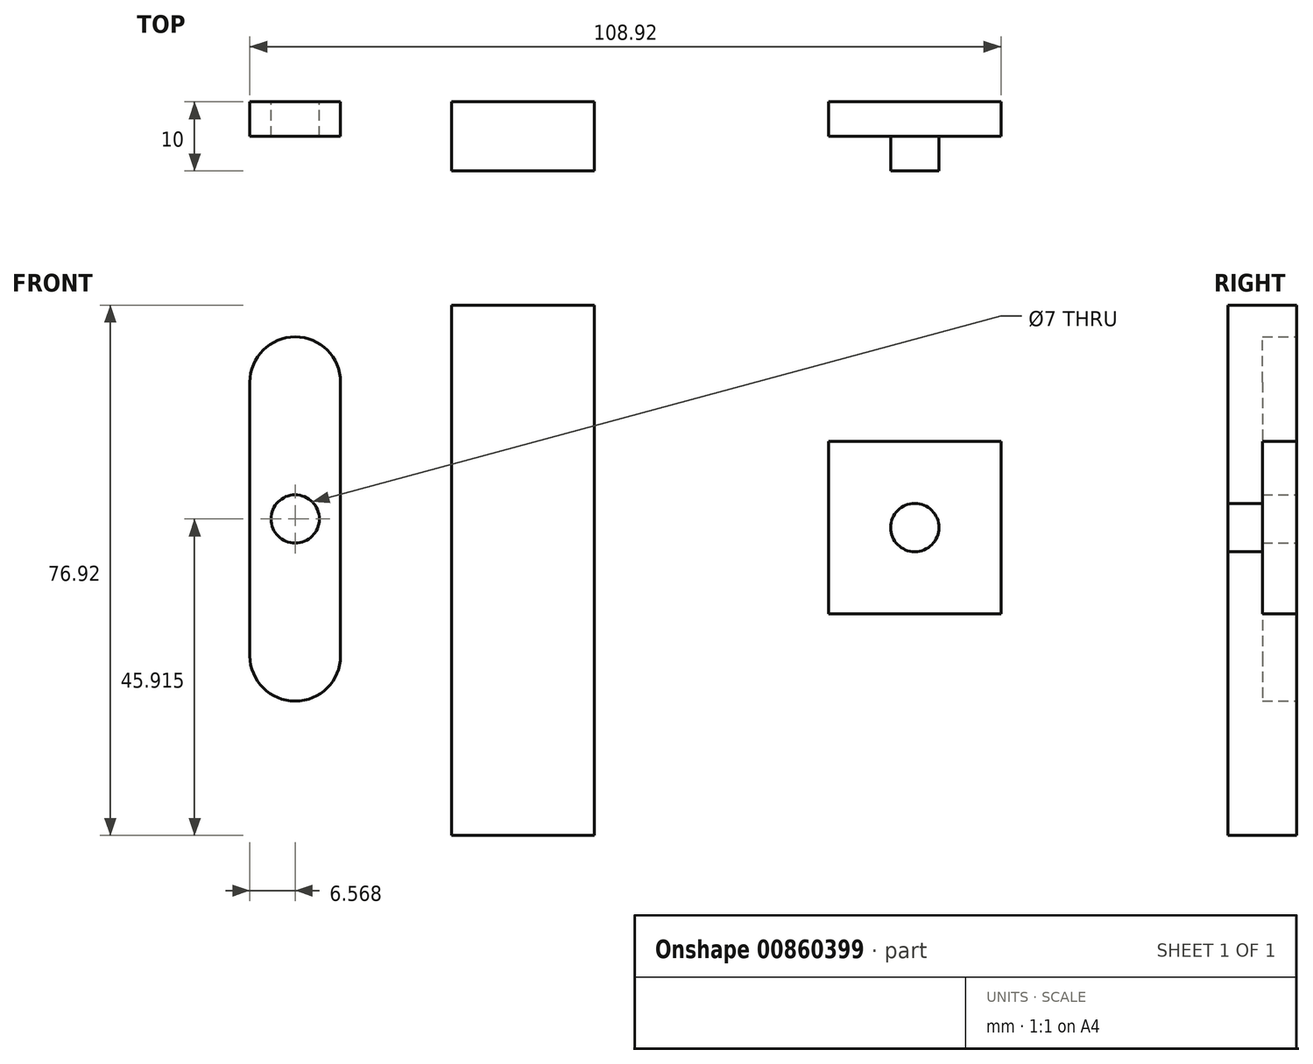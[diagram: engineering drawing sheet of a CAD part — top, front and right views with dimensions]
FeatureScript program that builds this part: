
annotation { "Feature Type Name" : "Feature", "Feature Type Description" : "" }
export const myFeature = defineFeature(function(context is Context, id is Id, definition is map)
    precondition{}
    {
        {
            var Q0;
            Q0=qCreatedBy(makeId("Front.planeOp"),FACE);
            var sketch = newSketch(context, id + "F0", { "sketchPlane" : qUnion([Q0])});
            skLineSegment(sketch, "E0", {"start": v(-60.7, 49.25) * mm, "end": v(-60.7, 9.54) * mm});
            skLineSegment(sketch, "E1", {"start": v(-60.7, 9.54) * mm, "end": v(-47.56, 9.54) * mm, "construction": true});
            skLineSegment(sketch, "E2", {"start": v(-47.56, 9.54) * mm, "end": v(-47.56, 49.25) * mm});
            skLineSegment(sketch, "E3", {"start": v(-47.56, 49.25) * mm, "end": v(-60.7, 49.25) * mm, "construction": true});
            skArc(sketch, "E4", {"start": v(-47.56, 49.25) * mm, "mid": v(-54.13, 55.82) * mm, "end": v(-60.7, 49.25) * mm});
            skArc(sketch, "E5", {"start": v(-60.7, 9.54) * mm, "mid": v(-54.13, 2.97) * mm, "end": v(-47.56, 9.54) * mm});
            skLineSegment(sketch, "E6", {"start": v(-60.7, 49.25) * mm, "end": v(-60.7, 29.4) * mm});
            skLineSegment(sketch, "E7", {"start": v(-60.7, 29.4) * mm, "end": v(-47.56, 29.4) * mm, "construction": true});
            skCircle(sketch, "E8", {"center": v(-54.13, 29.4) * mm, "radius": 3.5 * mm});
            skSolve(sketch);
        }
        {
            var Q0;
            Q0=makeQuery(id+"F0.imprint","IMPRINT",FACE,{"disambiguationData":[TD([[makeQuery(id+"F0.imprint","IMPRINT",EDGE,{"derivedFrom":sQuery(id+"F0.wireOp",EDGE,"E0")}),1.0]])]});
            extrude(context, id + "F1", {"entities" : qUnion([Q0]), "depth" : 5 * mm, "offsetDistance" : 25 * mm});
        }
        {
            var Q0;
            Q0=qCreatedBy(makeId("Front.planeOp"),FACE);
            var sketch = newSketch(context, id + "F2", { "sketchPlane" : qUnion([Q0])});
            skLineSegment(sketch, "E9.bottom", {"start": v(-31.43, 60.4) * mm, "end": v(-10.76, 60.4) * mm});
            skLineSegment(sketch, "E9.top", {"start": v(-31.43, -16.52) * mm, "end": v(-10.76, -16.52) * mm});
            skLineSegment(sketch, "E9.left", {"start": v(-31.43, 60.4) * mm, "end": v(-31.43, -16.52) * mm});
            skLineSegment(sketch, "E9.right", {"start": v(-10.76, 60.4) * mm, "end": v(-10.76, -16.52) * mm});
            skSolve(sketch);
        }
        {
            var Q0;
            Q0 = qSketchRegion(id + "F2", true);
            extrude(context, id + "F3", {"entities" : qUnion([Q0]), "depth" : 10 * mm, "offsetDistance" : 25 * mm});
        }
        {
            var Q0;
            Q0=qCreatedBy(makeId("Front.planeOp"),FACE);
            var sketch = newSketch(context, id + "F4", { "sketchPlane" : qUnion([Q0])});
            skLineSegment(sketch, "E10.bottom", {"start": v(23.22, 40.65) * mm, "end": v(48.22, 40.65) * mm});
            skLineSegment(sketch, "E10.top", {"start": v(23.22, 15.65) * mm, "end": v(48.22, 15.65) * mm});
            skLineSegment(sketch, "E10.left", {"start": v(23.22, 40.65) * mm, "end": v(23.22, 15.65) * mm});
            skLineSegment(sketch, "E10.right", {"start": v(48.22, 40.65) * mm, "end": v(48.22, 15.65) * mm});
            skLineSegment(sketch, "E11", {"start": v(23.22, 40.65) * mm, "end": v(48.22, 15.65) * mm});
            skLineSegment(sketch, "E12", {"start": v(23.22, 15.65) * mm, "end": v(48.22, 40.65) * mm});
            skCircle(sketch, "E13", {"center": v(35.72, 28.15) * mm, "radius": 3.5 * mm});
            skSolve(sketch);
        }
        {
            var Q0;
            {var subQ0=sQuery(id+"F4.wireOp",EDGE,"E10.bottom");Q0=makeQuery(id+"F4.imprint","IMPRINT",FACE,{"disambiguationData":[TD([[makeQuery(id+"F4.imprint","IMPRINT",EDGE,{"derivedFrom":subQ0}),-1.0]])]});}
            var Q1;
            {var subQ0=sQuery(id+"F4.wireOp",EDGE,"E10.left");Q1=makeQuery(id+"F4.imprint","IMPRINT",FACE,{"disambiguationData":[TD([[makeQuery(id+"F4.imprint","IMPRINT",EDGE,{"derivedFrom":subQ0}),1.0]])]});}
            var Q2;
            {var subQ0=sQuery(id+"F4.wireOp",EDGE,"E10.top");Q2=makeQuery(id+"F4.imprint","IMPRINT",FACE,{"disambiguationData":[TD([[makeQuery(id+"F4.imprint","IMPRINT",EDGE,{"derivedFrom":subQ0}),1.0]])]});}
            var Q3;
            {var subQ0=sQuery(id+"F4.wireOp",EDGE,"E10.right");Q3=makeQuery(id+"F4.imprint","IMPRINT",FACE,{"disambiguationData":[TD([[makeQuery(id+"F4.imprint","IMPRINT",EDGE,{"derivedFrom":subQ0}),-1.0]])]});}
            var Q4;
            {var subQ0=sQuery(id+"F4.wireOp",EDGE,"E13");var subQ1=sQuery(id+"F4.wireOp",EDGE,"E11");var subQ2=makeQuery(id+"F4.imprint","INTERSECT",VERTEX,{"disambiguationData":[OD(0.0)],"derivedFrom":[subQ1,subQ0]});Q4=makeQuery(id+"F4.imprint","IMPRINT",FACE,{"disambiguationData":[TD([[makeQuery(id+"F4.imprint","IMPRINT",EDGE,{"disambiguationData":[TD([[subQ2,-1.0]])],"derivedFrom":subQ1}),-1.0]])]});}
            var Q5;
            {var subQ0=sQuery(id+"F4.wireOp",EDGE,"E13");var subQ1=sQuery(id+"F4.wireOp",EDGE,"E11");var subQ2=makeQuery(id+"F4.imprint","INTERSECT",VERTEX,{"disambiguationData":[OD(0.0)],"derivedFrom":[subQ1,subQ0]});Q5=makeQuery(id+"F4.imprint","IMPRINT",FACE,{"disambiguationData":[TD([[makeQuery(id+"F4.imprint","IMPRINT",EDGE,{"disambiguationData":[TD([[subQ2,-1.0]])],"derivedFrom":subQ1}),1.0]])]});}
            var Q6;
            {var subQ0=sQuery(id+"F4.wireOp",EDGE,"E12");var subQ1=sQuery(id+"F4.wireOp",EDGE,"E11");var subQ2=makeQuery(id+"F4.imprint","INTERSECT",VERTEX,{"derivedFrom":[subQ1,subQ0]});Q6=makeQuery(id+"F4.imprint","IMPRINT",FACE,{"disambiguationData":[TD([[makeQuery(id+"F4.imprint","IMPRINT",EDGE,{"disambiguationData":[TD([[subQ2,-1.0]])],"derivedFrom":subQ1}),1.0]])]});}
            var Q7;
            {var subQ0=sQuery(id+"F4.wireOp",EDGE,"E12");var subQ1=sQuery(id+"F4.wireOp",EDGE,"E11");var subQ2=makeQuery(id+"F4.imprint","INTERSECT",VERTEX,{"derivedFrom":[subQ1,subQ0]});Q7=makeQuery(id+"F4.imprint","IMPRINT",FACE,{"disambiguationData":[TD([[makeQuery(id+"F4.imprint","IMPRINT",EDGE,{"disambiguationData":[TD([[subQ2,-1.0]])],"derivedFrom":subQ1}),-1.0]])]});}
            extrude(context, id + "F5", {"entities" : qUnion([Q0, Q1, Q2, Q3, Q4, Q5, Q6, Q7]), "depth" : 5 * mm, "offsetDistance" : 25 * mm});
        }
        {
            var Q0;
            {var subQ0=sQuery(id+"F4.wireOp",EDGE,"E13");var subQ1=sQuery(id+"F4.wireOp",EDGE,"E11");var subQ2=makeQuery(id+"F4.imprint","INTERSECT",VERTEX,{"disambiguationData":[OD(0.0)],"derivedFrom":[subQ1,subQ0]});Q0=makeQuery(id+"F4.imprint","IMPRINT",FACE,{"disambiguationData":[TD([[makeQuery(id+"F4.imprint","IMPRINT",EDGE,{"disambiguationData":[TD([[subQ2,-1.0]])],"derivedFrom":subQ1}),1.0]])]});}
            var Q1;
            {var subQ0=sQuery(id+"F4.wireOp",EDGE,"E12");var subQ1=sQuery(id+"F4.wireOp",EDGE,"E11");var subQ2=makeQuery(id+"F4.imprint","INTERSECT",VERTEX,{"derivedFrom":[subQ1,subQ0]});Q1=makeQuery(id+"F4.imprint","IMPRINT",FACE,{"disambiguationData":[TD([[makeQuery(id+"F4.imprint","IMPRINT",EDGE,{"disambiguationData":[TD([[subQ2,-1.0]])],"derivedFrom":subQ1}),1.0]])]});}
            var Q2;
            {var subQ0=sQuery(id+"F4.wireOp",EDGE,"E12");var subQ1=sQuery(id+"F4.wireOp",EDGE,"E11");var subQ2=makeQuery(id+"F4.imprint","INTERSECT",VERTEX,{"derivedFrom":[subQ1,subQ0]});Q2=makeQuery(id+"F4.imprint","IMPRINT",FACE,{"disambiguationData":[TD([[makeQuery(id+"F4.imprint","IMPRINT",EDGE,{"disambiguationData":[TD([[subQ2,-1.0]])],"derivedFrom":subQ1}),-1.0]])]});}
            var Q3;
            {var subQ0=sQuery(id+"F4.wireOp",EDGE,"E13");var subQ1=sQuery(id+"F4.wireOp",EDGE,"E11");var subQ2=makeQuery(id+"F4.imprint","INTERSECT",VERTEX,{"disambiguationData":[OD(0.0)],"derivedFrom":[subQ1,subQ0]});Q3=makeQuery(id+"F4.imprint","IMPRINT",FACE,{"disambiguationData":[TD([[makeQuery(id+"F4.imprint","IMPRINT",EDGE,{"disambiguationData":[TD([[subQ2,-1.0]])],"derivedFrom":subQ1}),-1.0]])]});}
            extrude(context, id + "F6", {"entities" : qUnion([Q0, Q1, Q2, Q3]), "operationType" : NewBodyOperationType.ADD, "depth" : 10 * mm, "offsetDistance" : 25 * mm});
        }
    });
